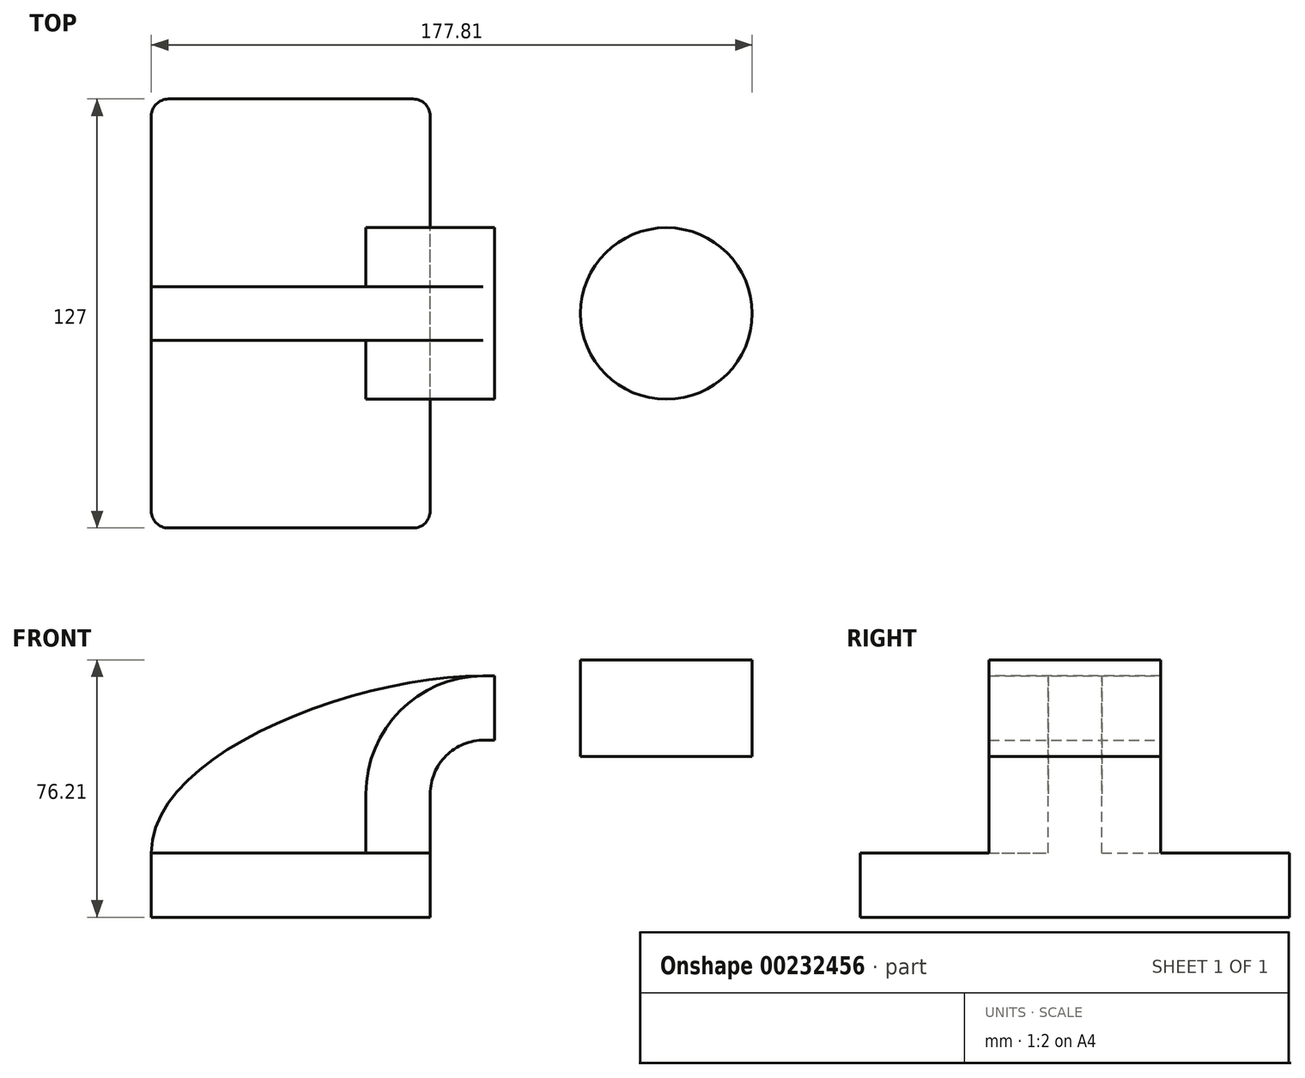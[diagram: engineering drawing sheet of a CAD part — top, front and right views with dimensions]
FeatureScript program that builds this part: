
annotation { "Feature Type Name" : "Feature", "Feature Type Description" : "" }
export const myFeature = defineFeature(function(context is Context, id is Id, definition is map)
    precondition{}
    {
        {
            var Q0;
            Q0=qCreatedBy(makeId("Front.planeOp"),FACE);
            var sketch = newSketch(context, id + "F0", { "sketchPlane" : qUnion([Q0])});
            skLineSegment(sketch, "E0.bottom", {"start": v(-41.28, -9.53) * mm, "end": v(41.28, -9.53) * mm});
            skLineSegment(sketch, "E0.top", {"start": v(-41.28, 9.53) * mm, "end": v(41.28, 9.53) * mm});
            skLineSegment(sketch, "E0.left", {"start": v(-41.28, -9.53) * mm, "end": v(-41.28, 9.53) * mm});
            skLineSegment(sketch, "E0.right", {"start": v(41.28, -9.53) * mm, "end": v(41.28, 9.53) * mm});
            skPoint(sketch, "E0.middle", {"position": v(0, 0) * mm});
            skLineSegment(sketch, "E1.bottom", {"start": v(60.33, 38.1) * mm, "end": v(111.13, 38.1) * mm});
            skLineSegment(sketch, "E1.top", {"start": v(60.33, 66.67) * mm, "end": v(111.13, 66.67) * mm});
            skLineSegment(sketch, "E1.left", {"start": v(60.33, 38.1) * mm, "end": v(60.33, 66.67) * mm});
            skLineSegment(sketch, "E1.right", {"start": v(111.13, 38.1) * mm, "end": v(111.13, 66.67) * mm});
            skPoint(sketch, "E1.middle", {"position": v(85.72, 52.39) * mm});
            skLineSegment(sketch, "E2", {"start": v(41.28, 9.53) * mm, "end": v(41.28, 27) * mm});
            skArc(sketch, "E3", {"start": v(41.28, 27) * mm, "mid": v(45.96, 38.26) * mm, "end": v(57.26, 42.88) * mm});
            skLineSegment(sketch, "E4", {"start": v(57.26, 42.88) * mm, "end": v(85.72, 42.88) * mm});
            skLineSegment(sketch, "E5.0", {"start": v(57.3, 61.93) * mm, "end": v(85.72, 61.93) * mm});
            skArc(sketch, "E5.1", {"start": v(22.23, 27) * mm, "mid": v(32.51, 51.75) * mm, "end": v(57.3, 61.93) * mm});
            skLineSegment(sketch, "E5.2", {"start": v(22.23, 9.53) * mm, "end": v(22.23, 27) * mm});
            skLineSegment(sketch, "E6", {"start": v(85.73, 38.1) * mm, "end": v(85.73, 66.67) * mm});
            skFitSpline(sketch, "E7", {"points": [v(-41.28, 9.52) * mm, v(57.3, 61.93) * mm], "startDerivative": vector(0, 88.35) * mm, "endDerivative": vector(115.8, 0) * mm});
            skSolve(sketch);
        }
        {
            var Q0;
            Q0=makeQuery(id+"F0.imprint","IMPRINT",FACE,{"disambiguationData":[TD([[makeQuery(id+"F0.imprint","IMPRINT",EDGE,{"derivedFrom":sQuery(id+"F0.wireOp",EDGE,"E0.bottom")}),1.0]])]});
            extrude(context, id + "F1", {"entities" : qUnion([Q0]), "endBound" : BoundingType.SYMMETRIC, "depth" : 127 * mm});
        }
        {
            var Q0;
            {var subQ1=sQuery(id+"F0.wireOp",EDGE,"E2");Q0=makeQuery(id+"F0.imprint","IMPRINT",FACE,{"disambiguationData":[TD([[makeQuery(id+"F0.imprint","IMPRINT",EDGE,{"derivedFrom":subQ1}),1.0]])]});}
            extrude(context, id + "F2", {"entities" : qUnion([Q0]), "operationType" : NewBodyOperationType.ADD, "endBound" : BoundingType.SYMMETRIC, "depth" : 50.8 * mm});
        }
        {
            var Q0;
            {var subQ3=sQuery(id+"F0.wireOp",EDGE,"E5.2");Q0=makeQuery(id+"F0.imprint","IMPRINT",FACE,{"disambiguationData":[TD([[makeQuery(id+"F0.imprint","IMPRINT",EDGE,{"derivedFrom":subQ3}),1.0]])]});}
            extrude(context, id + "F3", {"entities" : qUnion([Q0]), "operationType" : NewBodyOperationType.ADD, "endBound" : BoundingType.SYMMETRIC, "depth" : 15.88 * mm});
        }
        {
            var Q0;
            {var subQ0=sQuery(id+"F0.wireOp",EDGE,"E1.right");Q0=makeQuery(id+"F0.imprint","IMPRINT",FACE,{"disambiguationData":[TD([[makeQuery(id+"F0.imprint","IMPRINT",EDGE,{"derivedFrom":subQ0}),1.0]])]});}
            var Q1;
            Q1=sQuery(id+"F0.wireOp",EDGE,"E1.right");
            revolve(context, id + "F4", {"entities" : qUnion([Q0]), "axis" : qUnion([Q1]), "revolveType" : RevolveType.FULL});
        }
        {
            var Q0;
            Q0=makeQuery(id+"F1.opExtrude","CAP_EDGE",EDGE,{"disambiguationData":[OSD([sQuery(id+"F0.wireOp",EDGE,"E0.right")])],"isStart":false});
            var Q1;
            Q1=makeQuery(id+"F1.opExtrude","CAP_EDGE",EDGE,{"disambiguationData":[OSD([sQuery(id+"F0.wireOp",EDGE,"E0.left")])],"isStart":false});
            var Q2;
            Q2=makeQuery(id+"F1.opExtrude","CAP_EDGE",EDGE,{"disambiguationData":[OSD([sQuery(id+"F0.wireOp",EDGE,"E0.right")])],"isStart":true});
            var Q3;
            Q3=makeQuery(id+"F1.opExtrude","CAP_EDGE",EDGE,{"disambiguationData":[OSD([sQuery(id+"F0.wireOp",EDGE,"E0.left")])],"isStart":true});
            fillet(context, id + "F5", {"entities" : qUnion([Q0, Q1, Q2, Q3]), "radius" : 5.08 * mm, "tangentPropagation" : true, "allowEdgeOverflow" : false});
        }
    });
